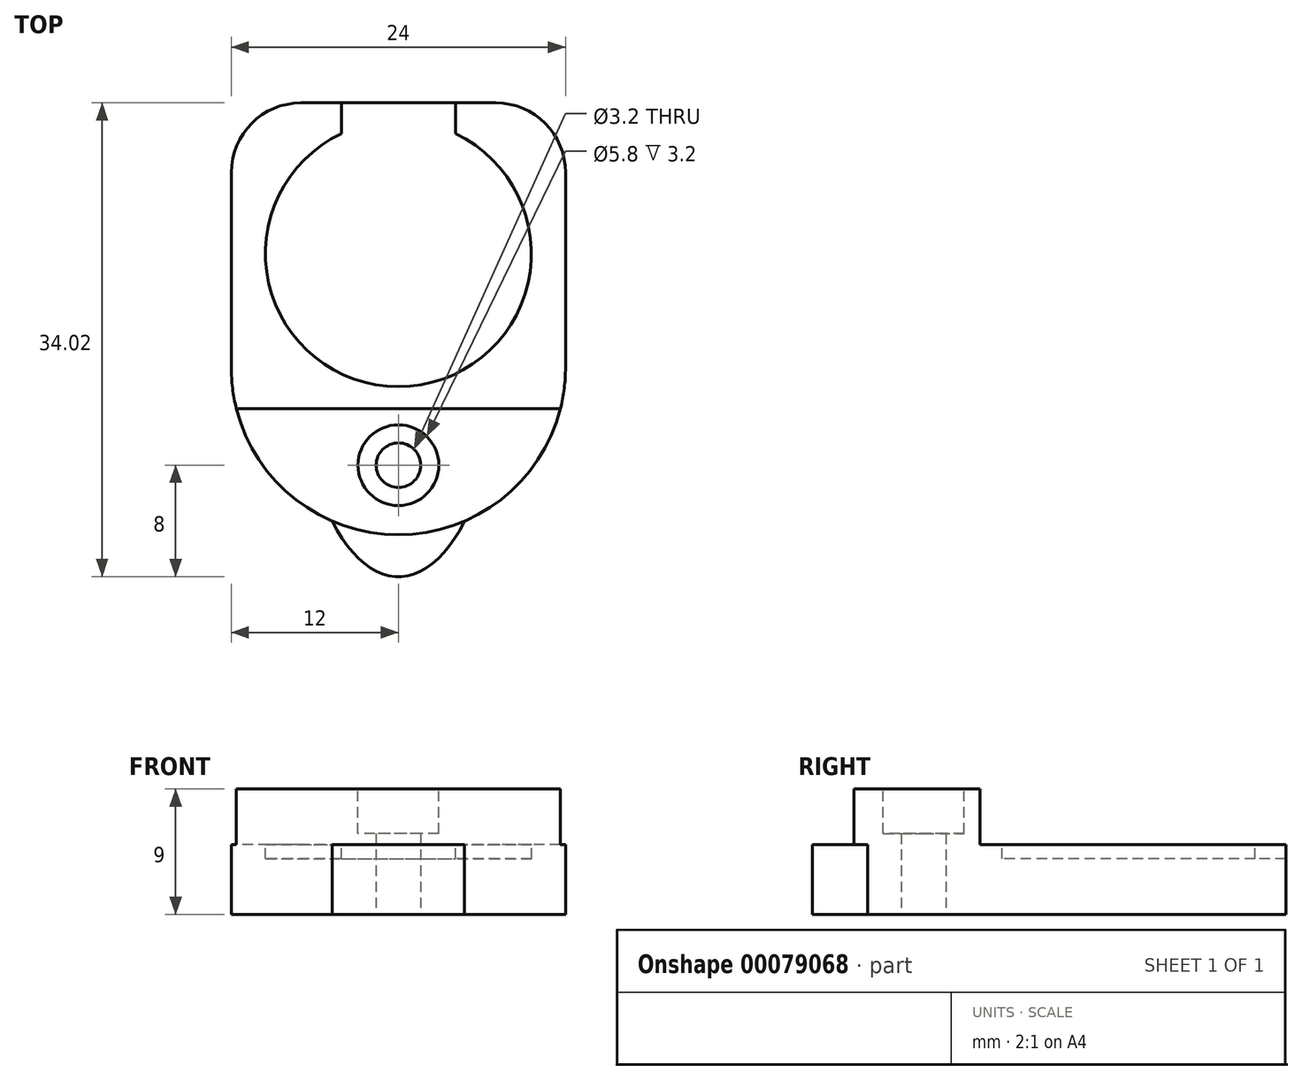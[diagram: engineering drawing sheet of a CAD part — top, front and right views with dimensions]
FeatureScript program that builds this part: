
annotation { "Feature Type Name" : "Feature", "Feature Type Description" : "" }
export const myFeature = defineFeature(function(context is Context, id is Id, definition is map)
    precondition{}
    {
        {
            var Q0;
            Q0=qCreatedBy(makeId("Top.planeOp"),FACE);
            var sketch = newSketch(context, id + "F0", { "sketchPlane" : qUnion([Q0])});
            skEllipse(sketch, "E0", {"center": v(0, 0) * mm, "majorRadius": 15 * mm, "minorRadius": 7 * mm, "majorAxis": v(0, -1)});
            skArc(sketch, "E1", {"start": v(2.1, 1.75) * mm, "mid": v(0, 3.85) * mm, "end": v(-2.1, 1.75) * mm});
            skPoint(sketch, "E2", {"position": v(0, -15) * mm});
            skPoint(sketch, "E3", {"position": v(0, 15) * mm});
            skArc(sketch, "E4", {"start": v(-2.1, -8.66) * mm, "mid": v(0, -10.76) * mm, "end": v(2.1, -8.66) * mm});
            skCircle(sketch, "E5", {"center": v(0, 9.46) * mm, "radius": 1.6 * mm});
            skLineSegment(sketch, "E6", {"start": v(-2.1, 1.75) * mm, "end": v(-2.1, -8.66) * mm});
            skLineSegment(sketch, "E7", {"start": v(2.1, 1.75) * mm, "end": v(2.1, -8.66) * mm});
            skPoint(sketch, "E7.startSnap0", {"position": v(7, 0) * mm});
            skSolve(sketch);
        }
        {
            var Q0;
            Q0=makeQuery(id+"F0.imprint","IMPRINT",FACE,{"disambiguationData":[TD([[makeQuery(id+"F0.imprint","IMPRINT",EDGE,{"derivedFrom":sQuery(id+"F0.wireOp",EDGE,"E0")}),1.0]])]});
            extrude(context, id + "F1", {"entities" : qUnion([Q0]), "depth" : 5 * mm});
        }
        {
            var Q0;
            Q0=makeQuery(id+"F1.opExtrude","CAP_FACE",FACE,{"disambiguationData":[OSD([sQuery(id+"F0.wireOp",EDGE,"E0"),sQuery(id+"F0.wireOp",EDGE,"E1"),sQuery(id+"F0.wireOp",EDGE,"E4"),sQuery(id+"F0.wireOp",EDGE,"E5"),sQuery(id+"F0.wireOp",EDGE,"E6"),sQuery(id+"F0.wireOp",EDGE,"E7")])],"isStart":false});
            var sketch = newSketch(context, id + "F2", { "sketchPlane" : qUnion([Q0])});
            skCircle(sketch, "E8.cCircle", {"center": v(0, 9.46) * mm, "radius": 2.75 * mm, "construction": true});
            skLineSegment(sketch, "E8.0", {"start": v(3.18, 9.47) * mm, "end": v(1.6, 6.71) * mm});
            skLineSegment(sketch, "E8.1", {"start": v(1.6, 6.71) * mm, "end": v(-1.58, 6.7) * mm});
            skLineSegment(sketch, "E8.2", {"start": v(-1.58, 6.7) * mm, "end": v(-3.18, 9.44) * mm});
            skLineSegment(sketch, "E8.3", {"start": v(-3.18, 9.44) * mm, "end": v(-1.6, 12.2) * mm});
            skLineSegment(sketch, "E8.4", {"start": v(-1.6, 12.2) * mm, "end": v(1.58, 12.21) * mm});
            skLineSegment(sketch, "E8.5", {"start": v(1.58, 12.21) * mm, "end": v(3.18, 9.47) * mm});
            skPoint(sketch, "E8.0.midPoint", {"position": v(2.39, 8.1) * mm});
            skSolve(sketch);
        }
        {
            var Q0;
            Q0 = qSketchRegion(id + "F2", true);
            extrude(context, id + "F3", {"entities" : qUnion([Q0]), "operationType" : NewBodyOperationType.REMOVE, "oppositeDirection" : true, "depth" : 2.5 * mm});
        }
        {
            var Q0;
            Q0=qCreatedBy(makeId("Top.planeOp"),FACE);
            var sketch = newSketch(context, id + "F4", { "sketchPlane" : qUnion([Q0])});
            skArc(sketch, "E9", {"start": v(-12, 0) * mm, "mid": v(0, -12) * mm, "end": v(12, 0) * mm});
            skLineSegment(sketch, "E10", {"start": v(-12, 0) * mm, "end": v(-12, 14.02) * mm});
            skLineSegment(sketch, "E11", {"start": v(-7, 19.02) * mm, "end": v(7, 19.02) * mm});
            skLineSegment(sketch, "E12", {"start": v(12, 14.02) * mm, "end": v(12, 0) * mm});
            skCircle(sketch, "E13", {"center": v(0, -7) * mm, "radius": 1.6 * mm});
            skPoint(sketch, "E14.visualSharp", {"position": v(-12, 19.02) * mm});
            skArc(sketch, "E14.filletArc", {"start": v(-7, 19.02) * mm, "mid": v(-10.54, 17.55) * mm, "end": v(-12, 14.02) * mm});
            skPoint(sketch, "E15.visualSharp", {"position": v(12, 19.02) * mm});
            skArc(sketch, "E15.filletArc", {"start": v(12, 14.02) * mm, "mid": v(10.54, 17.55) * mm, "end": v(7, 19.02) * mm});
            skSolve(sketch);
        }
        {
            var Q0;
            Q0 = qSketchRegion(id + "F4", true);
            extrude(context, id + "F5", {"entities" : qUnion([Q0]), "depth" : 5 * mm});
        }
        {
            var Q0;
            Q0=makeQuery(id+"F5.opExtrude","CAP_FACE",FACE,{"disambiguationData":[OSD([sQuery(id+"F4.wireOp",EDGE,"E9"),sQuery(id+"F4.wireOp",EDGE,"E10"),sQuery(id+"F4.wireOp",EDGE,"E11"),sQuery(id+"F4.wireOp",EDGE,"E12"),sQuery(id+"F4.wireOp",EDGE,"E13"),sQuery(id+"F4.wireOp",EDGE,"E14.filletArc"),sQuery(id+"F4.wireOp",EDGE,"E15.filletArc")])],"isStart":false});
            var sketch = newSketch(context, id + "F6", { "sketchPlane" : qUnion([Q0])});
            skLineSegment(sketch, "E16", {"start": v(-11.63, -2.95) * mm, "end": v(11.63, -2.95) * mm});
            skArc(sketch, "E17", {"start": v(-11.63, -2.95) * mm, "mid": v(0, -12) * mm, "end": v(11.63, -2.95) * mm});
            skCircle(sketch, "E18", {"center": v(0, -7) * mm, "radius": 1.6 * mm});
            skSolve(sketch);
        }
        {
            var Q0;
            Q0 = qSketchRegion(id + "F6", true);
            extrude(context, id + "F7", {"entities" : qUnion([Q0]), "operationType" : NewBodyOperationType.ADD, "depth" : 4 * mm});
        }
        {
            var Q0;
            Q0=makeQuery(id+"F5.opExtrude","CAP_FACE",FACE,{"disambiguationData":[OSD([sQuery(id+"F4.wireOp",EDGE,"E9"),sQuery(id+"F4.wireOp",EDGE,"E10"),sQuery(id+"F4.wireOp",EDGE,"E11"),sQuery(id+"F4.wireOp",EDGE,"E12"),sQuery(id+"F4.wireOp",EDGE,"E13"),sQuery(id+"F4.wireOp",EDGE,"E14.filletArc"),sQuery(id+"F4.wireOp",EDGE,"E15.filletArc")])],"isStart":false});
            var sketch = newSketch(context, id + "F8", { "sketchPlane" : qUnion([Q0])});
            skArc(sketch, "E19", {"start": v(-4.1, 16.81) * mm, "mid": v(0, -1.36) * mm, "end": v(4.1, 16.81) * mm});
            skLineSegment(sketch, "E20", {"start": v(0, 19.02) * mm, "end": v(4.1, 19.02) * mm});
            skLineSegment(sketch, "E21", {"start": v(4.1, 19.02) * mm, "end": v(4.1, 16.81) * mm});
            skLineSegment(sketch, "E22.MirrorCS", {"start": v(0, 19.02) * mm, "end": v(-4.1, 19.02) * mm});
            skLineSegment(sketch, "E23.MirrorCS", {"start": v(-4.1, 19.02) * mm, "end": v(-4.1, 16.81) * mm});
            skSolve(sketch);
        }
        {
            var Q0;
            Q0 = qSketchRegion(id + "F8", true);
            extrude(context, id + "F9", {"entities" : qUnion([Q0]), "operationType" : NewBodyOperationType.REMOVE, "oppositeDirection" : true, "depth" : 1 * mm});
        }
        {
            var Q0;
            Q0=makeQuery(id+"F7.opExtrude","CAP_FACE",FACE,{"disambiguationData":[OSD([sQuery(id+"F6.wireOp",EDGE,"E16"),sQuery(id+"F6.wireOp",EDGE,"E17"),sQuery(id+"F6.wireOp",EDGE,"E18")])],"isStart":false});
            var sketch = newSketch(context, id + "F10", { "sketchPlane" : qUnion([Q0])});
            skCircle(sketch, "E24", {"center": v(0, -7) * mm, "radius": 2.9 * mm});
            skSolve(sketch);
        }
        {
            var Q0;
            Q0 = qSketchRegion(id + "F10", true);
            extrude(context, id + "F11", {"entities" : qUnion([Q0]), "operationType" : NewBodyOperationType.REMOVE, "oppositeDirection" : true, "depth" : 3.2 * mm});
        }
    });
